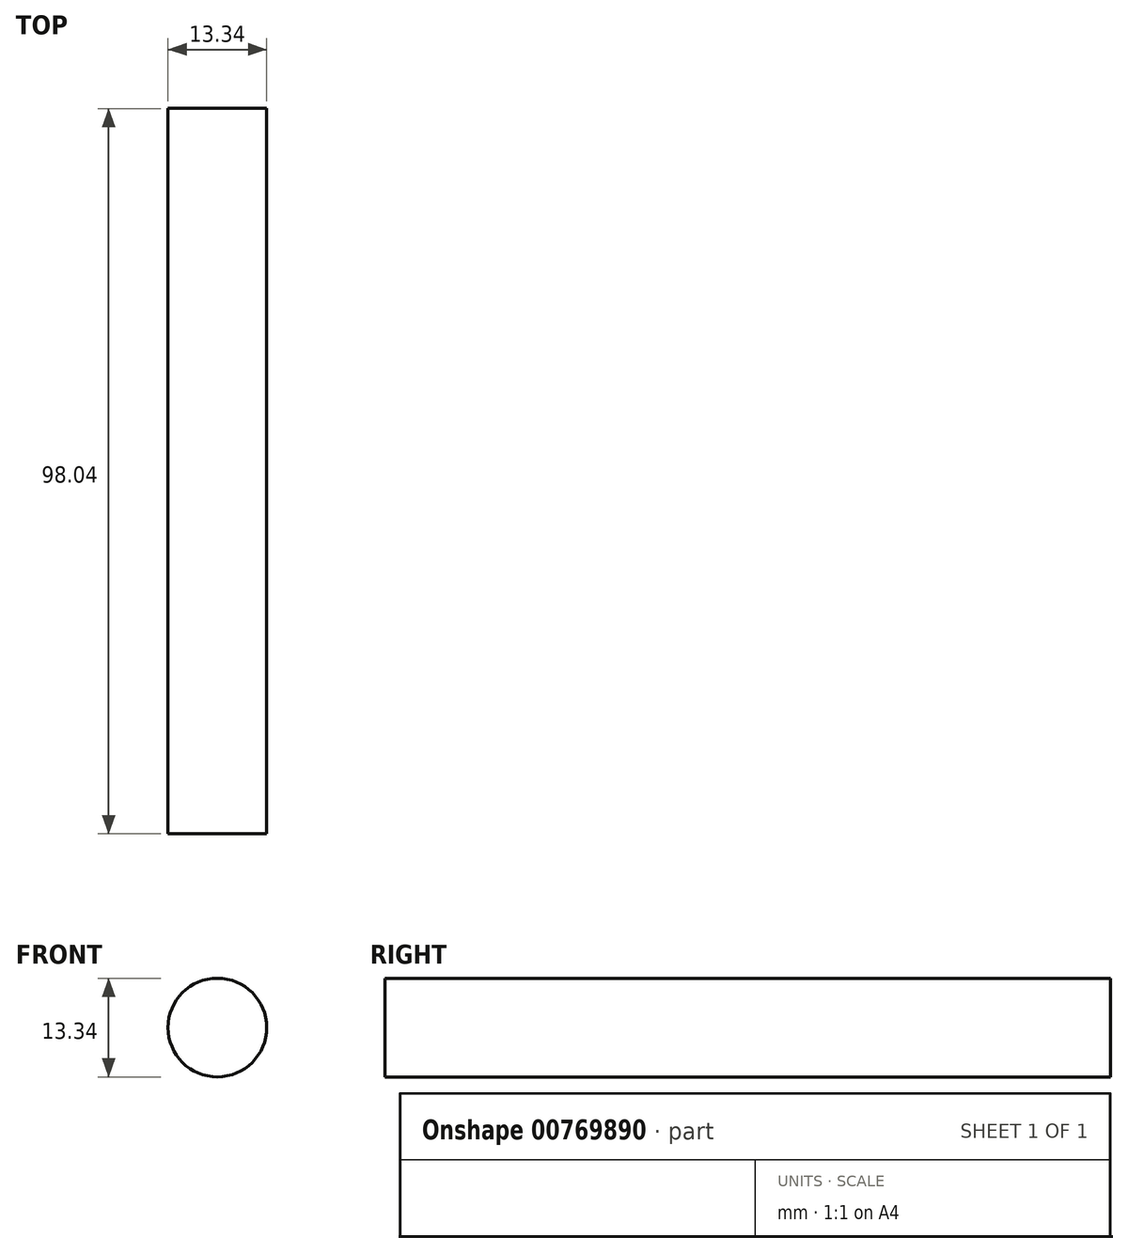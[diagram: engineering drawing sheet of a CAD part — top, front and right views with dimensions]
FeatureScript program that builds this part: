
annotation { "Feature Type Name" : "Feature", "Feature Type Description" : "" }
export const myFeature = defineFeature(function(context is Context, id is Id, definition is map)
    precondition{}
    {
        {
            var Q0;
            Q0=qCreatedBy(makeId("Front.planeOp"),FACE);
            var sketch = newSketch(context, id + "F0", { "sketchPlane" : qUnion([Q0])});
            skCircle(sketch, "E0", {"center": v(0, 0) * mm, "radius": 6.67 * mm});
            skSolve(sketch);
        }
        {
            var Q0;
            Q0 = qSketchRegion(id + "F0", true);
            extrude(context, id + "F1", {"entities" : qUnion([Q0]), "endBound" : BoundingType.SYMMETRIC, "depth" : 98.04 * mm, "offsetDistance" : 25.4 * mm});
        }
    });
